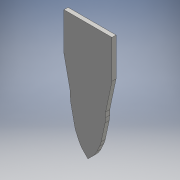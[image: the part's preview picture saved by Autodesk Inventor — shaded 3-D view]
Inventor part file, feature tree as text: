
AUTODESK INVENTOR PART (.ipt)
format: ipt  version: 2016 (Build 200138000, 138)  size: 119,808 bytes
history: native  units: mm
features: fillet x3, other x1, extrude x1, sketch x1
ambient origin geometry x8: Origin, YZ Plane, XZ Plane, XY Plane, X Axis, Y Axis, Z Axis, Center Point
bodies: Body1 (feature_tree)
feature tree (6):
  other  "Sólido1"
  extrude  "Extrusión1"  Depth=50.0mm
  fillet  "Empalme1"  Radius=50.0mm
  fillet  "Empalme2"  Radius=50.0mm
  fillet  "Empalme3"  [1 undecoded]
  sketch  "Boceto1"  dims[d12=9.0mm d13=0.0mm d14=50.0mm d15=50.0mm d16=50.0mm]
note: 1 required parameter value undecoded (feature->parameter linkage not recoverable at this tier; creation-order binding heuristic only, values carry confidence <= 0.55)
